# Revit family: NAU_Naughtone_Stng_Ruby_StarBases1
name_source: partatom
category: Furniture
revit_build: Autodesk Revit 2018 (Build: 20170223_1515(x64)
units: mm (PartAtom-declared; Revit-internal decimal feet)

## family parameters
Always vertical = Yes
Cut with Voids When Loaded = No
OmniClass Number = 23.40.20.00
OmniClass Title = General Furniture and Specialties
Room Calculation Point = No
Shared = Yes
Work Plane-Based = No

## types (2) — shared parameters
Assembly Code = E2020200
AssetType = Movable
BIMObjectName = NAU_Naughtone_Seating_Ruby_StarBase
Category = Pr_40_50_12 : Chairs, seats and benches
Color = Various
DurationUnit = year
Finish = Plastic Shell in 8 RAL colours
IfcExportAs = IfcFurnishingElementType
IfcExportType = CHAIR
Keynote = Pr_40_50_12
MainColor = Various
ManufacturerAddress = Knaresborough Tech Park, Manse Lane, Knaresborough, HG5 8LF
ManufacturerName = Naughtone
ManufacturerURL = www.naughtone.com
Material = Steel/plastic
NBSDescription = Seating
NBSReference = 45-35-72/352
Name = Seating_Ruby_StarBase_Naughtone
NominalHeight = 795 mm  [stored 2.60827 ft]
ProductInformation = www.naughtone.com/products/ruby/
Revision = 1
Shape = Rectangular
SustainabilityPerformance = FSC certified. FISP certified. ISO 14001
URL = www.naughtone.com
Uniclass2015Code = Pr_40_50_12
Uniclass2015Title = Chairs, seats and benches
Version = 1
WarrantyDescription = Request warranty information from naughtone
WarrantyDurationLabor = 7
WarrantyDurationParts = 7
WarrantyDurationUnit = year

## per-type parameters (varying)
| type | Description | Has4StarBase | Has5StarBase | Model | ModelNumber | ModelReference | NominalLength | NominalWidth | Size |
| Ruby Chair 4 Star Base_RUBYCH4S | Ruby Chair 4 Star Base | Yes | No | RUBYCH4S | RUBYCH4S | Ruby Chair 4 Star Base | 610 mm | 530 mm | 610 x 530 x 795mm |
| Ruby Chair 5 Star Base_RUBYCH5S | Ruby Chair 5 Star Base | No | Yes | RUBYCH5S | RUBYCH5S | Ruby Chair 5 Star Base | 635 mm | 635 mm | 635 x 635 x 795mm |

note: [stored X ft] marks values corroborated as IEEE doubles in the binary element streams (Revit-internal decimal feet)

## geometry (parser evidence)
native form markers: Sweep x5
no freeform markers — native parametric forms only
